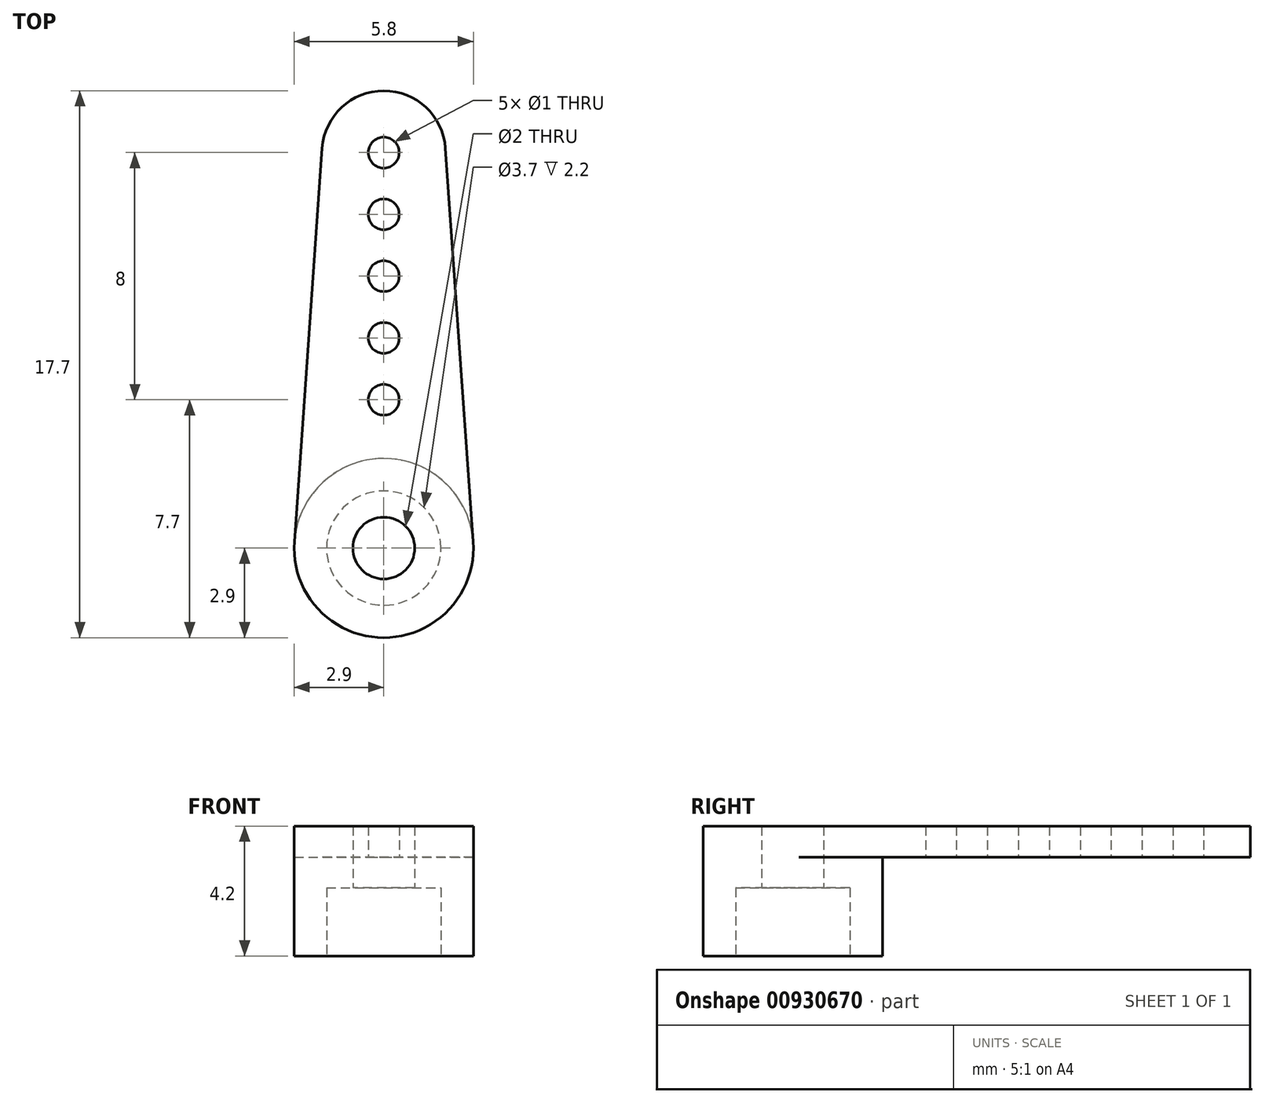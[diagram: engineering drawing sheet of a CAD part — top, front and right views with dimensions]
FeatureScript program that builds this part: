
annotation { "Feature Type Name" : "Feature", "Feature Type Description" : "" }
export const myFeature = defineFeature(function(context is Context, id is Id, definition is map)
    precondition{}
    {
        {
            var Q0;
            Q0=qCreatedBy(makeId("Top.planeOp"),FACE);
            var sketch = newSketch(context, id + "F0", { "sketchPlane" : qUnion([Q0])});
            skCircle(sketch, "E0", {"center": v(0, 0) * mm, "radius": 1 * mm});
            skArc(sketch, "E1", {"start": v(-2.9, 0.2) * mm, "mid": v(0, -2.9) * mm, "end": v(2.9, 0.2) * mm});
            skLineSegment(sketch, "E2", {"start": v(-2.9, 0.2) * mm, "end": v(-2, 12.94) * mm});
            skLineSegment(sketch, "E3", {"start": v(2.9, 0.2) * mm, "end": v(2, 12.94) * mm});
            skArc(sketch, "E4", {"start": v(2, 12.94) * mm, "mid": v(0, 14.8) * mm, "end": v(-2, 12.94) * mm});
            skCircle(sketch, "E5", {"center": v(0, 12.8) * mm, "radius": 0.5 * mm});
            skCircle(sketch, "E6", {"center": v(0, 10.8) * mm, "radius": 0.5 * mm});
            skCircle(sketch, "E7", {"center": v(0, 8.8) * mm, "radius": 0.5 * mm});
            skCircle(sketch, "E8", {"center": v(0, 6.8) * mm, "radius": 0.5 * mm});
            skCircle(sketch, "E9", {"center": v(0, 4.8) * mm, "radius": 0.5 * mm});
            skSolve(sketch);
        }
        {
            var Q0;
            Q0=qSketchRegion(id+"F0",true);
            extrude(context, id + "F1", {"entities" : qUnion([Q0]), "depth" : 4.2 * mm, "offsetDistance" : 25 * mm});
        }
        {
            var Q0;
            Q0=makeQuery(id+"F1.opExtrude","CAP_FACE",FACE,{"disambiguationData":[OSD([sQuery(id+"F0.wireOp",EDGE,"E0"),sQuery(id+"F0.wireOp",EDGE,"E1"),sQuery(id+"F0.wireOp",EDGE,"E2"),sQuery(id+"F0.wireOp",EDGE,"E3"),sQuery(id+"F0.wireOp",EDGE,"E4"),sQuery(id+"F0.wireOp",EDGE,"E5"),sQuery(id+"F0.wireOp",EDGE,"E6"),sQuery(id+"F0.wireOp",EDGE,"E7"),sQuery(id+"F0.wireOp",EDGE,"E8"),sQuery(id+"F0.wireOp",EDGE,"E9")])],"isStart":true});
            var sketch = newSketch(context, id + "F2", { "sketchPlane" : qUnion([Q0])});
            skArc(sketch, "E10", {"start": v(-2.9, -0.2) * mm, "mid": v(0, -2.9) * mm, "end": v(2.9, -0.2) * mm});
            skLineSegment(sketch, "E11", {"start": v(-2.9, -0.2) * mm, "end": v(-2, -12.94) * mm});
            skLineSegment(sketch, "E12", {"start": v(2.9, -0.2) * mm, "end": v(2, -12.94) * mm});
            skArc(sketch, "E13", {"start": v(-2, -12.94) * mm, "mid": v(0, -14.8) * mm, "end": v(2, -12.94) * mm});
            skSolve(sketch);
        }
        {
            var Q0;
            Q0=qSketchRegion(id+"F2",true);
            extrude(context, id + "F3", {"entities" : qUnion([Q0]), "operationType" : NewBodyOperationType.REMOVE, "oppositeDirection" : true, "depth" : 3.2 * mm, "offsetDistance" : 25 * mm});
        }
        {
            var Q0;
            Q0=makeQuery(id+"F1.opExtrude","CAP_FACE",FACE,{"disambiguationData":[OSD([sQuery(id+"F0.wireOp",EDGE,"E0"),sQuery(id+"F0.wireOp",EDGE,"E1"),sQuery(id+"F0.wireOp",EDGE,"E2"),sQuery(id+"F0.wireOp",EDGE,"E3"),sQuery(id+"F0.wireOp",EDGE,"E4"),sQuery(id+"F0.wireOp",EDGE,"E5"),sQuery(id+"F0.wireOp",EDGE,"E6"),sQuery(id+"F0.wireOp",EDGE,"E7"),sQuery(id+"F0.wireOp",EDGE,"E8"),sQuery(id+"F0.wireOp",EDGE,"E9")])],"isStart":true});
            var sketch = newSketch(context, id + "F4", { "sketchPlane" : qUnion([Q0])});
            skCircle(sketch, "E14", {"center": v(0, 0) * mm, "radius": 1.85 * mm});
            skCircle(sketch, "E15", {"center": v(0, 0) * mm, "radius": 1 * mm});
            skSolve(sketch);
        }
        {
            var Q0;
            Q0=qSketchRegion(id+"F4",true);
            extrude(context, id + "F5", {"entities" : qUnion([Q0]), "operationType" : NewBodyOperationType.REMOVE, "oppositeDirection" : true, "depth" : 2.2 * mm, "offsetDistance" : 25 * mm});
        }
    });
